# Revit family: Specialty_Equipment-Bavis_Fabacraft-Manual_Transaction_Drawer_Counter-BD2 NEW
name_source: partatom
category: Specialty Equipment
units: mm (PartAtom-declared; Revit-internal decimal feet)

## family parameters
Always vertical = Yes
Cut with Voids When Loaded = Yes
Host = Wall
OmniClass Number = 23.40.70.27.24.21
OmniClass Title = Service and Teller Window Units
Part Type = Normal
Room Calculation Point = No
Round Connector Dimension = Use Diameter
Shared = No

## types (1)
- BD2
    Apparent Load = 0 VA
    Assembly Code = E1010
    C Back = 0' - 3 7/16"
    C Control Box Height = 1' - 2 3/4"
    C Counter Open Length = 0' - 11"
    C Counter Open Width = 1' - 3 3/4"
    C Door Height = 0' - 9 3/8"
    C Door Width = 0' - 11 3/4"
    C Drawer = 0' - 0"
    C Inset = 0' - 0"
    C Middle = 1' - 3 3/4"
    C Rough Height = 0' - 10 3/4"
    C Rough Width = 1' - 4"
    C Sign Constraint = 2
    C Start = 0' - 9 1/2"
    C Stroke = 1' - 4 1/2"
    C Void Start = 0' - 8 1/2"
    Counter Top = Counter - Bavis Fabacraft - Almond
    Default Elevation = 0' - 0"
    Description = Manual Transaction Drawer with Counter
    Drawer = Paint - Bavis Fabacraft - Red
    Elevation Height = 3' - 0"
    Glazing = Plastic - Bavis Fabacraft - Clear
    Hardware = Metal - Bavis Fabacraft - Aluminum - Dark Grey
    Height = 1' - 1 15/16"
    Instruction Sheet Link = https://docs.bavis.com
    Keynote = 14 90 00
    Length = 2' - 5 3/16"
    Load Classification = Power
    Manufacturer = Bavis Fabacraft
    Model = See Order Code
    Number of Poles = 1
    Power Factor = 1
    Product Documentation Link = https://docs.bavis.com
    Product Name = Bavis Manual Transaction Drawer with Counter
    Product Page URL = https://www.bavis.com
    URL = https://www.bavis.com
    Version = 2020 - v1.0a
    Video Link = https://www.youtube.com
    Voltage = 120 V
    Width = 2' - 8"

## geometry (parser evidence)
native form markers: Sweep x3
no freeform markers — native parametric forms only
